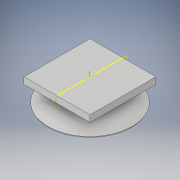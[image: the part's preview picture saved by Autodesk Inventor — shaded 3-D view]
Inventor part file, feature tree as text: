
AUTODESK INVENTOR PART (.ipt)
format: ipt  version: 2019.1 (Build 231200000, 200)  size: 141,824 bytes
history: native  units: mm
features: sketch x3, other x2, extrude x1, revolve x1
ambient origin geometry x8: Origin, YZ Plane, XZ Plane, XY Plane, X Axis, Y Axis, Z Axis, Center Point
bodies: Body1 (feature_tree)
feature tree (7):
  other  "ソリッド1"
  extrude  "押し出し1"  Depth=1000.0mm
  other  "作業平面1"
  sketch  "スケッチ3"
  revolve  "回転1"
  sketch  "スケッチ1"
  sketch  "スケッチ4"
